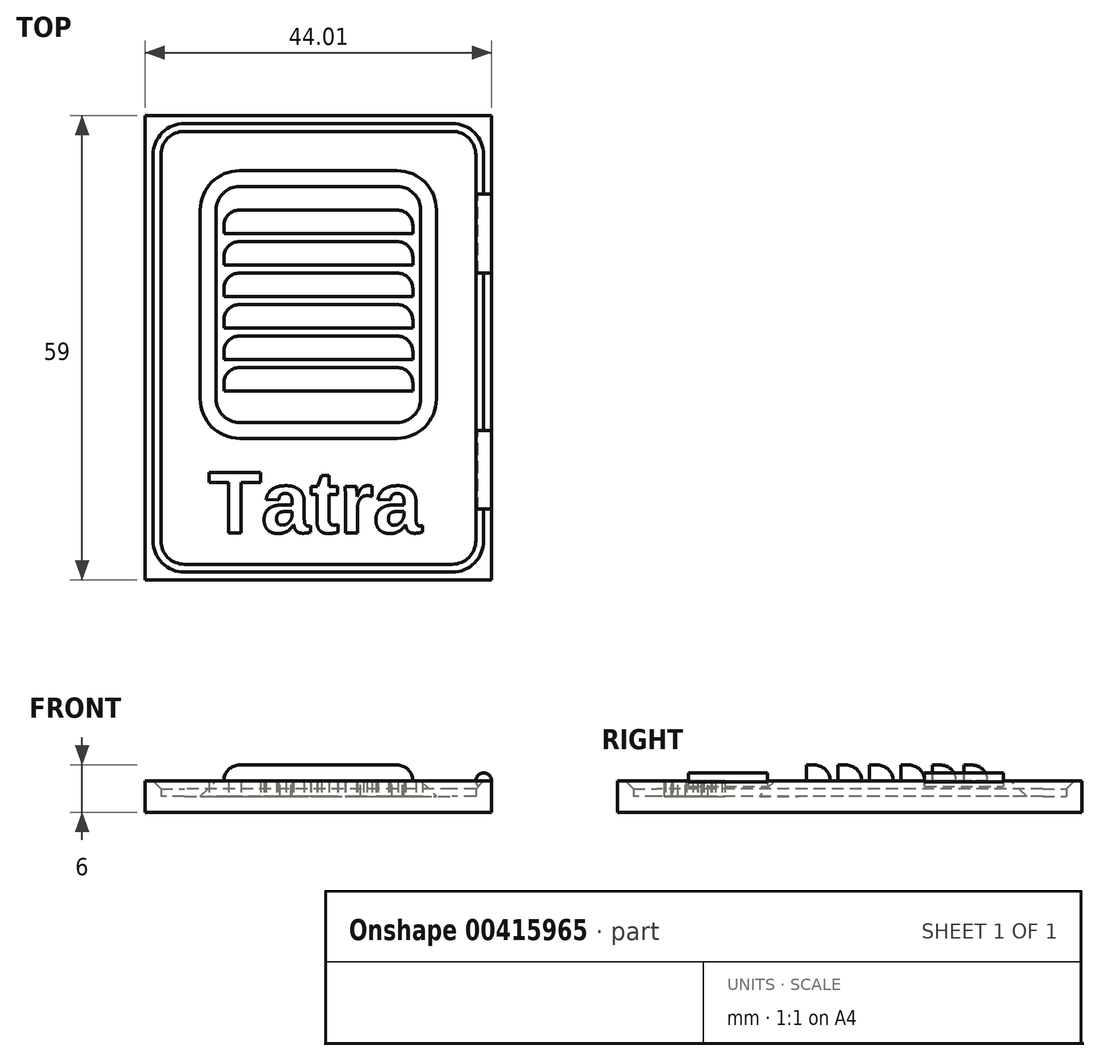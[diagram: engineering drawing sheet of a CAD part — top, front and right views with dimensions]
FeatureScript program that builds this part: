
annotation { "Feature Type Name" : "Feature", "Feature Type Description" : "" }
export const myFeature = defineFeature(function(context is Context, id is Id, definition is map)
    precondition{}
    {
        {
            var Q0;
            Q0=qCreatedBy(makeId("Top.planeOp"),FACE);
            var sketch = newSketch(context, id + "F0", { "sketchPlane" : qUnion([Q0])});
            skLineSegment(sketch, "E0.bottom", {"start": v(-26.46, 17) * mm, "end": v(17.54, 17) * mm});
            skLineSegment(sketch, "E0.top", {"start": v(-26.46, -42) * mm, "end": v(17.54, -42) * mm});
            skLineSegment(sketch, "E0.left", {"start": v(-26.46, 17) * mm, "end": v(-26.46, -42) * mm});
            skLineSegment(sketch, "E0.right", {"start": v(17.54, 17) * mm, "end": v(17.54, -42) * mm});
            skSolve(sketch);
        }
        {
            var Q0;
            Q0=qSketchRegion(id+"F0",true);
            extrude(context, id + "F1", {"entities" : qUnion([Q0]), "depth" : 2 * mm, "offsetDistance" : 25 * mm});
        }
        {
            var Q0;
            Q0=makeQuery(id+"F1.opExtrude","CAP_FACE",FACE,{"disambiguationData":[OSD([sQuery(id+"F0.wireOp",EDGE,"E0.bottom"),sQuery(id+"F0.wireOp",EDGE,"E0.top"),sQuery(id+"F0.wireOp",EDGE,"E0.left"),sQuery(id+"F0.wireOp",EDGE,"E0.right")])],"isStart":false});
            var sketch = newSketch(context, id + "F2", { "sketchPlane" : qUnion([Q0])});
            skLineSegment(sketch, "E1.bottom", {"start": v(-26.46, 17) * mm, "end": v(17.54, 17) * mm});
            skLineSegment(sketch, "E1.top", {"start": v(-26.46, -42) * mm, "end": v(17.54, -42) * mm});
            skLineSegment(sketch, "E1.left", {"start": v(-26.46, 17) * mm, "end": v(-26.46, -42) * mm});
            skLineSegment(sketch, "E1.right", {"start": v(17.54, 17) * mm, "end": v(17.54, -42) * mm});
            skLineSegment(sketch, "E2.0", {"start": v(-24.46, 15) * mm, "end": v(-24.46, -40) * mm});
            skLineSegment(sketch, "E3.0", {"start": v(-24.46, 15) * mm, "end": v(15.54, 15) * mm});
            skLineSegment(sketch, "E4.0", {"start": v(15.54, 15) * mm, "end": v(15.54, -40) * mm});
            skLineSegment(sketch, "E5.0", {"start": v(-24.46, -40) * mm, "end": v(15.54, -40) * mm});
            skPoint(sketch, "E6", {"position": v(15.54, -22.21) * mm});
            skText(sketch, "E7", { "text": "Tatra", "fontName": "Arimo-Bold.ttf"});
            const initialGuessF2  = {"E7": [-0.02196, -0.038, 1, 0, 0.01]};
            skSetInitialGuess(sketch, initialGuessF2);
            skSolve(sketch);
        }
        {
            var Q0;
            Q0=qSketchRegion(id+"F2",true);
            extrude(context, id + "F3", {"entities" : qUnion([Q0]), "operationType" : NewBodyOperationType.ADD, "depth" : 2 * mm, "offsetDistance" : 25 * mm});
        }
        {
            var Q0;
            Q0=makeQuery(id+"F1.opExtrude","CAP_FACE",FACE,{"disambiguationData":[OSD([sQuery(id+"F0.wireOp",EDGE,"E0.bottom"),sQuery(id+"F0.wireOp",EDGE,"E0.top"),sQuery(id+"F0.wireOp",EDGE,"E0.left"),sQuery(id+"F0.wireOp",EDGE,"E0.right")])],"isStart":false});
            var sketch = newSketch(context, id + "F4", { "sketchPlane" : qUnion([Q0])});
            skLineSegment(sketch, "E8.bottom", {"start": v(-14.46, 10) * mm, "end": v(5.54, 10) * mm});
            skLineSegment(sketch, "E8.top", {"start": v(-14.46, -24) * mm, "end": v(5.54, -24) * mm});
            skLineSegment(sketch, "E8.left", {"start": v(-19.46, 5) * mm, "end": v(-19.46, -19) * mm});
            skLineSegment(sketch, "E8.right", {"start": v(10.54, 5) * mm, "end": v(10.54, -19) * mm});
            skPoint(sketch, "E9.visualSharp", {"position": v(-19.46, 10) * mm});
            skArc(sketch, "E9.filletArc", {"start": v(-14.46, 10) * mm, "mid": v(-18, 8.53) * mm, "end": v(-19.46, 5) * mm});
            skPoint(sketch, "E10.visualSharp", {"position": v(10.54, 10) * mm});
            skArc(sketch, "E10.filletArc", {"start": v(10.54, 5) * mm, "mid": v(9.08, 8.53) * mm, "end": v(5.54, 10) * mm});
            skPoint(sketch, "E11.visualSharp", {"position": v(10.54, -24) * mm});
            skArc(sketch, "E11.filletArc", {"start": v(5.54, -24) * mm, "mid": v(9.08, -22.54) * mm, "end": v(10.54, -19) * mm});
            skPoint(sketch, "E12.visualSharp", {"position": v(-19.46, -24) * mm});
            skArc(sketch, "E12.filletArc", {"start": v(-19.46, -19) * mm, "mid": v(-18, -22.54) * mm, "end": v(-14.46, -24) * mm});
            skSolve(sketch);
        }
        {
            var Q0;
            Q0=makeQuery(id+"F4.imprint","IMPRINT",FACE,{"disambiguationData":[TD([[makeQuery(id+"F4.imprint","IMPRINT",EDGE,{"derivedFrom":sQuery(id+"F4.wireOp",EDGE,"E8.bottom")}),-1.0]])]});
            extrude(context, id + "F5", {"entities" : qUnion([Q0]), "operationType" : NewBodyOperationType.ADD, "depth" : 2 * mm, "offsetDistance" : 25 * mm});
        }
        {
            var Q0;
            Q0=makeQuery(id+"F5.opExtrude","CAP_FACE",FACE,{"disambiguationData":[OSD([sQuery(id+"F4.wireOp",EDGE,"E8.bottom"),sQuery(id+"F4.wireOp",EDGE,"E8.top"),sQuery(id+"F4.wireOp",EDGE,"E8.left"),sQuery(id+"F4.wireOp",EDGE,"E8.right"),sQuery(id+"F4.wireOp",EDGE,"E9.filletArc"),sQuery(id+"F4.wireOp",EDGE,"E10.filletArc"),sQuery(id+"F4.wireOp",EDGE,"E11.filletArc"),sQuery(id+"F4.wireOp",EDGE,"E12.filletArc")])],"isStart":false});
            var sketch = newSketch(context, id + "F6", { "sketchPlane" : qUnion([Q0])});
            skLineSegment(sketch, "E13.bottom", {"start": v(-14.46, 5) * mm, "end": v(5.54, 5) * mm});
            skLineSegment(sketch, "E13.left", {"start": v(-16.46, 3) * mm, "end": v(-16.46, 2) * mm});
            skLineSegment(sketch, "E13.right", {"start": v(7.54, 3) * mm, "end": v(7.54, 2) * mm});
            skLineSegment(sketch, "E14.0", {"start": v(-14.46, 1) * mm, "end": v(5.54, 1) * mm});
            skLineSegment(sketch, "E15.0", {"start": v(-14.46, -3) * mm, "end": v(5.54, -3) * mm});
            skLineSegment(sketch, "E16.0", {"start": v(-14.46, -7) * mm, "end": v(5.54, -7) * mm});
            skLineSegment(sketch, "E17.0", {"start": v(-14.46, -11) * mm, "end": v(5.54, -11) * mm});
            skPoint(sketch, "E18", {"position": v(-16.46, 1) * mm});
            skPoint(sketch, "E19", {"position": v(-16.46, -3) * mm});
            skPoint(sketch, "E20", {"position": v(-16.46, -7) * mm});
            skPoint(sketch, "E21", {"position": v(-16.46, -11) * mm});
            skPoint(sketch, "E22", {"position": v(-16.46, -15) * mm});
            skPoint(sketch, "E23", {"position": v(7.54, 5) * mm});
            skPoint(sketch, "E24", {"position": v(7.54, 1) * mm});
            skPoint(sketch, "E25", {"position": v(7.54, -3) * mm});
            skPoint(sketch, "E26", {"position": v(7.54, -7) * mm});
            skPoint(sketch, "E27", {"position": v(7.54, -11) * mm});
            skPoint(sketch, "E28", {"position": v(7.54, -15) * mm});
            skPoint(sketch, "E29", {"position": v(-16.46, 5) * mm});
            skLineSegment(sketch, "E30.0", {"start": v(-16.46, 2) * mm, "end": v(7.54, 2) * mm});
            skLineSegment(sketch, "E31.0", {"start": v(-16.46, -2) * mm, "end": v(7.54, -2) * mm});
            skLineSegment(sketch, "E32.0", {"start": v(-16.46, -6) * mm, "end": v(7.54, -6) * mm});
            skLineSegment(sketch, "E33.0", {"start": v(-16.46, -10) * mm, "end": v(7.54, -10) * mm});
            skLineSegment(sketch, "E34.0", {"start": v(-16.46, -14) * mm, "end": v(7.54, -14) * mm});
            skLineSegment(sketch, "E35", {"start": v(-14.46, -15) * mm, "end": v(5.54, -15) * mm});
            skLineSegment(sketch, "E36.trimOffspring", {"start": v(-16.46, -1) * mm, "end": v(-16.46, -2) * mm});
            skLineSegment(sketch, "E37.trimOffspring", {"start": v(-16.46, -5) * mm, "end": v(-16.46, -6) * mm});
            skLineSegment(sketch, "E38.trimOffspring", {"start": v(-16.46, -9) * mm, "end": v(-16.46, -10) * mm});
            skLineSegment(sketch, "E39.trimOffspring", {"start": v(-16.46, -13) * mm, "end": v(-16.46, -14) * mm});
            skLineSegment(sketch, "E40.0", {"start": v(-16.46, -18) * mm, "end": v(7.54, -18) * mm});
            skLineSegment(sketch, "E41.trimOffspring", {"start": v(7.54, -17) * mm, "end": v(7.54, -18) * mm});
            skLineSegment(sketch, "E42.trimOffspring", {"start": v(-16.46, -17) * mm, "end": v(-16.46, -18) * mm});
            skLineSegment(sketch, "E43.trimOffspring", {"start": v(7.54, -13) * mm, "end": v(7.54, -14) * mm});
            skLineSegment(sketch, "E44.trimOffspring", {"start": v(7.54, -9) * mm, "end": v(7.54, -10) * mm});
            skLineSegment(sketch, "E45.trimOffspring", {"start": v(7.54, -5) * mm, "end": v(7.54, -6) * mm});
            skLineSegment(sketch, "E46.trimOffspring", {"start": v(7.54, -1) * mm, "end": v(7.54, -2) * mm});
            skArc(sketch, "E47.filletArc", {"start": v(-14.46, 5) * mm, "mid": v(-15.87, 4.4) * mm, "end": v(-16.46, 3) * mm});
            skArc(sketch, "E48.filletArc", {"start": v(7.54, 3) * mm, "mid": v(6.96, 4.4) * mm, "end": v(5.54, 5) * mm});
            skArc(sketch, "E49.filletArc", {"start": v(-14.46, 1) * mm, "mid": v(-15.87, 0.4) * mm, "end": v(-16.46, -1) * mm});
            skArc(sketch, "E50.filletArc", {"start": v(-14.46, -3) * mm, "mid": v(-15.87, -3.6) * mm, "end": v(-16.46, -5) * mm});
            skArc(sketch, "E51.filletArc", {"start": v(-14.46, -7) * mm, "mid": v(-15.87, -7.6) * mm, "end": v(-16.46, -9) * mm});
            skArc(sketch, "E52.filletArc", {"start": v(-14.46, -11) * mm, "mid": v(-15.87, -11.6) * mm, "end": v(-16.46, -13) * mm});
            skArc(sketch, "E53.filletArc", {"start": v(-14.46, -15) * mm, "mid": v(-15.87, -15.6) * mm, "end": v(-16.46, -17) * mm});
            skArc(sketch, "E54.filletArc", {"start": v(7.54, -17) * mm, "mid": v(6.96, -15.6) * mm, "end": v(5.54, -15) * mm});
            skArc(sketch, "E55.filletArc", {"start": v(7.54, -13) * mm, "mid": v(6.96, -11.6) * mm, "end": v(5.54, -11) * mm});
            skArc(sketch, "E56.filletArc", {"start": v(7.54, -9) * mm, "mid": v(6.96, -7.6) * mm, "end": v(5.54, -7) * mm});
            skArc(sketch, "E57.filletArc", {"start": v(7.54, -5) * mm, "mid": v(6.96, -3.6) * mm, "end": v(5.54, -3) * mm});
            skArc(sketch, "E58.filletArc", {"start": v(7.54, -1) * mm, "mid": v(6.96, 0.4) * mm, "end": v(5.54, 1) * mm});
            skSolve(sketch);
        }
        {
            var Q0;
            Q0=makeQuery(id+"F6.imprint","IMPRINT",FACE,{"disambiguationData":[TD([[makeQuery(id+"F6.imprint","IMPRINT",EDGE,{"derivedFrom":sQuery(id+"F6.wireOp",EDGE,"E14.0")}),-1.0]])]});
            var Q1;
            Q1=makeQuery(id+"F6.imprint","IMPRINT",FACE,{"disambiguationData":[TD([[makeQuery(id+"F6.imprint","IMPRINT",EDGE,{"derivedFrom":sQuery(id+"F6.wireOp",EDGE,"E15.0")}),-1.0]])]});
            var Q2;
            Q2=makeQuery(id+"F6.imprint","IMPRINT",FACE,{"disambiguationData":[TD([[makeQuery(id+"F6.imprint","IMPRINT",EDGE,{"derivedFrom":sQuery(id+"F6.wireOp",EDGE,"E16.0")}),-1.0]])]});
            var Q3;
            Q3=makeQuery(id+"F6.imprint","IMPRINT",FACE,{"disambiguationData":[TD([[makeQuery(id+"F6.imprint","IMPRINT",EDGE,{"derivedFrom":sQuery(id+"F6.wireOp",EDGE,"E17.0")}),-1.0]])]});
            var Q4;
            Q4=makeQuery(id+"F6.imprint","IMPRINT",FACE,{"disambiguationData":[TD([[makeQuery(id+"F6.imprint","IMPRINT",EDGE,{"derivedFrom":sQuery(id+"F6.wireOp",EDGE,"E35")}),-1.0]])]});
            var Q5;
            Q5=makeQuery(id+"F6.imprint","IMPRINT",FACE,{"disambiguationData":[TD([[makeQuery(id+"F6.imprint","IMPRINT",EDGE,{"derivedFrom":sQuery(id+"F6.wireOp",EDGE,"E13.bottom")}),-1.0]])]});
            extrude(context, id + "F7", {"entities" : qUnion([Q0, Q1, Q2, Q3, Q4, Q5]), "operationType" : NewBodyOperationType.ADD, "depth" : 2 * mm, "offsetDistance" : 25 * mm});
        }
        {
            var Q0;
            Q0=qCreatedBy(makeId("Front.planeOp"),FACE);
            cPlane(context, id + "F8", {"entities" : qUnion([Q0]), "cplaneType" : CPlaneType.OFFSET, "offset" : 28 * mm, "width" : 150 * mm, "height" : 150 * mm});
        }
        {
            var Q0;
            Q0=qCreatedBy(id+"F8.planeOp",FACE);
            var sketch = newSketch(context, id + "F9", { "sketchPlane" : qUnion([Q0])});
            skCircle(sketch, "E59", {"center": v(16.55, 3.98) * mm, "radius": 1 * mm});
            skPoint(sketch, "E60.center.orphan", {"position": v(14.24, 3.98) * mm});
            skSolve(sketch);
        }
        {
            var Q0;
            Q0=qSketchRegion(id+"F9",true);
            extrude(context, id + "F10", {"entities" : qUnion([Q0]), "operationType" : NewBodyOperationType.ADD, "endBound" : BoundingType.SYMMETRIC, "depth" : 10 * mm, "offsetDistance" : 25 * mm});
        }
        {
            var Q0;
            Q0=qCreatedBy(id+"F8.planeOp",FACE);
            cPlane(context, id + "F11", {"entities" : qUnion([Q0]), "cplaneType" : CPlaneType.OFFSET, "offset" : 30 * mm, "oppositeDirection" : true, "width" : 150 * mm, "height" : 150 * mm});
        }
        {
            var Q0;
            Q0=qCreatedBy(id+"F11.planeOp",FACE);
            var sketch = newSketch(context, id + "F12", { "sketchPlane" : qUnion([Q0])});
            skCircle(sketch, "E61", {"center": v(16.55, 4) * mm, "radius": 1 * mm});
            skSolve(sketch);
        }
        {
            var Q0;
            Q0=qSketchRegion(id+"F12",true);
            extrude(context, id + "F13", {"entities" : qUnion([Q0]), "operationType" : NewBodyOperationType.ADD, "endBound" : BoundingType.SYMMETRIC, "depth" : 10 * mm, "offsetDistance" : 25 * mm});
        }
        {
            var Q0;
            Q0=makeQuery(id+"F5.opExtrude","CAP_EDGE",EDGE,{"disambiguationData":[OSD([sQuery(id+"F4.wireOp",EDGE,"E8.top")])],"isStart":false});
            chamfer(context, id + "F14", {"entities" : qUnion([Q0]), "width" : 2 * mm, "tangentPropagation" : true});
        }
        {
            var Q0;
            Q0=makeQuery(id+"F3.opExtrude","SWEPT_EDGE",EDGE,{"disambiguationData":[OSD([sQuery(id+"F2.wireOp",EDGE,"E2.0"),sQuery(id+"F2.wireOp",EDGE,"E3.0")])]});
            var Q1;
            Q1=makeQuery(id+"F3.opExtrude","SWEPT_EDGE",EDGE,{"disambiguationData":[OSD([sQuery(id+"F2.wireOp",EDGE,"E2.0"),sQuery(id+"F2.wireOp",EDGE,"E5.0")])]});
            var Q2;
            Q2=makeQuery(id+"F3.opExtrude","SWEPT_EDGE",EDGE,{"disambiguationData":[OSD([sQuery(id+"F2.wireOp",EDGE,"E4.0"),sQuery(id+"F2.wireOp",EDGE,"E5.0")])]});
            var Q3;
            Q3=makeQuery(id+"F3.opExtrude","SWEPT_EDGE",EDGE,{"disambiguationData":[OSD([sQuery(id+"F2.wireOp",EDGE,"E3.0"),sQuery(id+"F2.wireOp",EDGE,"E4.0")])]});
            fillet(context, id + "F15", {"entities" : qUnion([Q0, Q1, Q2, Q3]), "radius" : 3 * mm, "tangentPropagation" : true, "allowEdgeOverflow" : false});
        }
        {
            var Q0;
            Q0=makeQuery(id+"F3.opExtrude","CAP_EDGE",EDGE,{"disambiguationData":[OSD([sQuery(id+"F2.wireOp",EDGE,"E2.0")])],"isStart":false});
            chamfer(context, id + "F16", {"entities" : qUnion([Q0]), "width" : 1 * mm, "tangentPropagation" : true});
        }
        {
            var Q0;
            Q0=makeQuery(id+"F7.opExtrude","CAP_EDGE",EDGE,{"disambiguationData":[OSD([sQuery(id+"F6.wireOp",EDGE,"E13.bottom")])],"isStart":false});
            var Q1;
            Q1=makeQuery(id+"F7.opExtrude","CAP_EDGE",EDGE,{"disambiguationData":[OSD([sQuery(id+"F6.wireOp",EDGE,"E14.0")])],"isStart":false});
            var Q2;
            Q2=makeQuery(id+"F7.opExtrude","CAP_EDGE",EDGE,{"disambiguationData":[OSD([sQuery(id+"F6.wireOp",EDGE,"E15.0")])],"isStart":false});
            var Q3;
            Q3=makeQuery(id+"F7.opExtrude","CAP_EDGE",EDGE,{"disambiguationData":[OSD([sQuery(id+"F6.wireOp",EDGE,"E16.0")])],"isStart":false});
            var Q4;
            Q4=makeQuery(id+"F7.opExtrude","CAP_EDGE",EDGE,{"disambiguationData":[OSD([sQuery(id+"F6.wireOp",EDGE,"E17.0")])],"isStart":false});
            var Q5;
            Q5=makeQuery(id+"F7.opExtrude","CAP_EDGE",EDGE,{"disambiguationData":[OSD([sQuery(id+"F6.wireOp",EDGE,"E35")])],"isStart":false});
            fillet(context, id + "F17", {"entities" : qUnion([Q0, Q1, Q2, Q3, Q4, Q5]), "radius" : 2 * mm, "tangentPropagation" : true, "allowEdgeOverflow" : false});
        }
        {
            var Q0;
            Q0=qSketchRegion(id+"F2",true);
            extrude(context, id + "F18", {"entities" : qUnion([Q0]), "operationType" : NewBodyOperationType.ADD, "depth" : 1 * mm, "offsetDistance" : 25 * mm});
        }
        {
            var Q0;
            Q0=makeQuery(id+"F1.opExtrude","CAP_FACE",FACE,{"disambiguationData":[OSD([sQuery(id+"F0.wireOp",EDGE,"E0.bottom"),sQuery(id+"F0.wireOp",EDGE,"E0.top"),sQuery(id+"F0.wireOp",EDGE,"E0.left"),sQuery(id+"F0.wireOp",EDGE,"E0.right")])],"isStart":false});
            var sketch = newSketch(context, id + "F19", { "sketchPlane" : qUnion([Q0])});
            skText(sketch, "E62", { "text": "Tatra", "fontName": "Arimo-Bold.ttf"});
            const initialGuessF19  = {"E62": [-0.01846, -0.036, 1, 0, 0.008]};
            skSetInitialGuess(sketch, initialGuessF19);
            skSolve(sketch);
        }
        {
            var Q0;
            Q0=makeQuery(id+"F19.imprint","IMPRINT",FACE,{"disambiguationData":[TD([[makeQuery(id+"F19.imprint","IMPRINT",EDGE,{"derivedFrom":sQuery(id+"F19.wireOp",EDGE,"E62.sketch_text.stroke-0")}),-1.0]])]});
            var Q1;
            Q1=makeQuery(id+"F19.imprint","IMPRINT",FACE,{"disambiguationData":[TD([[makeQuery(id+"F19.imprint","IMPRINT",EDGE,{"derivedFrom":sQuery(id+"F19.wireOp",EDGE,"E62.sketch_text.stroke-8")}),-1.0]])]});
            var Q2;
            Q2=makeQuery(id+"F19.imprint","IMPRINT",FACE,{"disambiguationData":[TD([[makeQuery(id+"F19.imprint","IMPRINT",EDGE,{"derivedFrom":sQuery(id+"F19.wireOp",EDGE,"E62.sketch_text.stroke-46")}),-1.0]])]});
            var Q3;
            Q3=makeQuery(id+"F19.imprint","IMPRINT",FACE,{"disambiguationData":[TD([[makeQuery(id+"F19.imprint","IMPRINT",EDGE,{"derivedFrom":sQuery(id+"F19.wireOp",EDGE,"E62.sketch_text.stroke-64")}),-1.0]])]});
            var Q4;
            Q4=makeQuery(id+"F19.imprint","IMPRINT",FACE,{"disambiguationData":[TD([[makeQuery(id+"F19.imprint","IMPRINT",EDGE,{"derivedFrom":sQuery(id+"F19.wireOp",EDGE,"E62.sketch_text.stroke-81")}),-1.0]])]});
            extrude(context, id + "F20", {"entities" : qUnion([Q0, Q1, Q2, Q3, Q4]), "operationType" : NewBodyOperationType.ADD, "depth" : 2 * mm, "offsetDistance" : 25 * mm});
        }
    });
